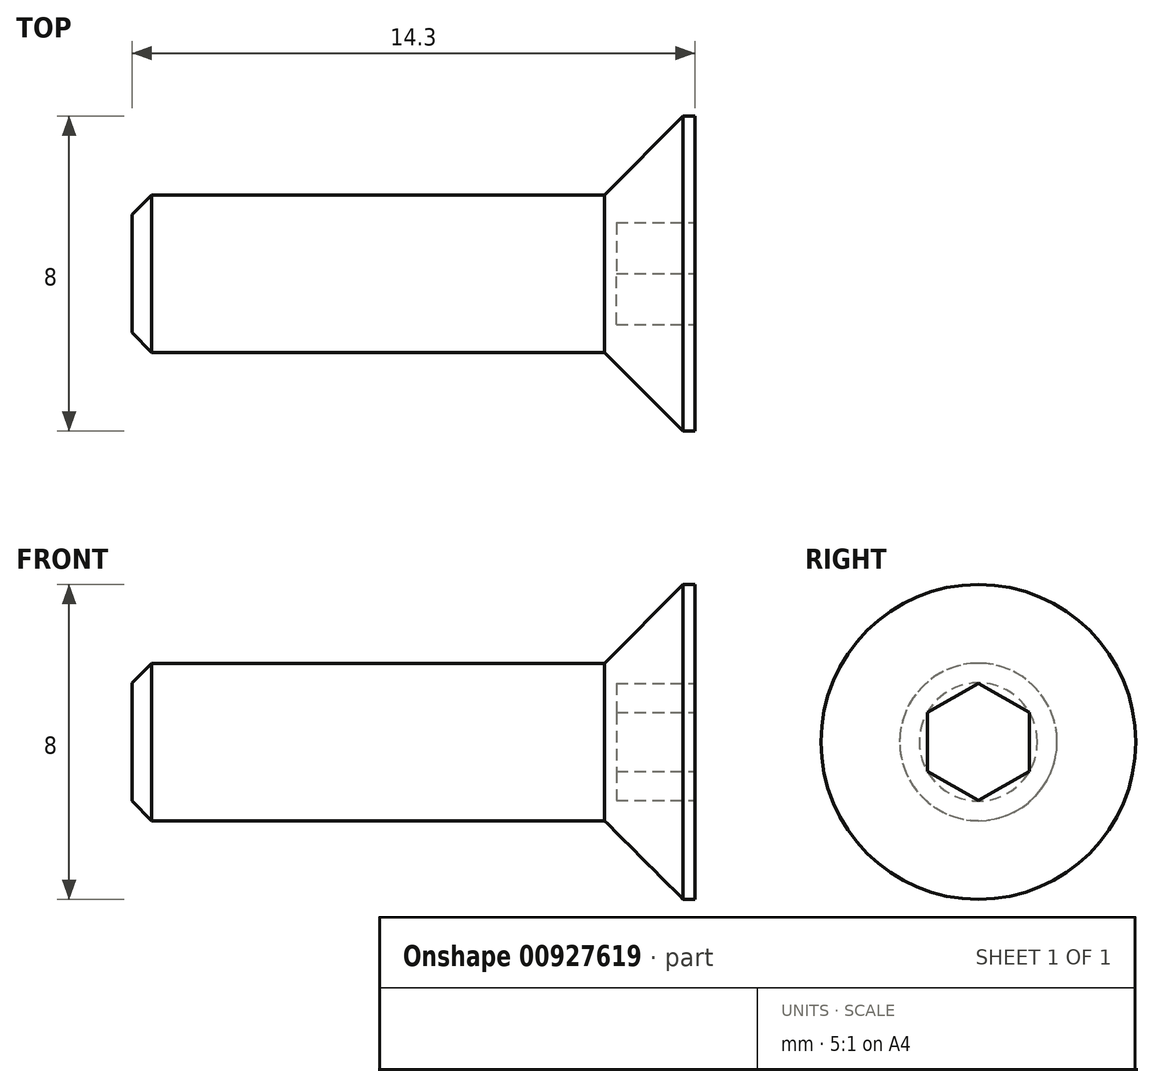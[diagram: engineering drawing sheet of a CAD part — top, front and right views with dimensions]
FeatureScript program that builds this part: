
annotation { "Feature Type Name" : "Feature", "Feature Type Description" : "" }
export const myFeature = defineFeature(function(context is Context, id is Id, definition is map)
    precondition{}
    {
        {
            var Q0;
            Q0=qCreatedBy(makeId("Right.planeOp"),FACE);
            var sketch = newSketch(context, id + "F0", { "sketchPlane" : qUnion([Q0])});
            skCircle(sketch, "E0", {"center": v(0, 0) * mm, "radius": 4 * mm});
            skSolve(sketch);
        }
        {
            var Q0;
            Q0 = qSketchRegion(id + "F0", true);
            extrude(context, id + "F1", {"entities" : qUnion([Q0]), "oppositeDirection" : true, "depth" : 2.3 * mm, "offsetDistance" : 25 * mm});
        }
        {
            var Q0;
            Q0=makeQuery(id+"F1.opExtrude","CAP_FACE",FACE,{"disambiguationData":[OSD([sQuery(id+"F0.wireOp",EDGE,"E0")])],"isStart":false});
            var sketch = newSketch(context, id + "F2", { "sketchPlane" : qUnion([Q0])});
            skCircle(sketch, "E1", {"center": v(0, 0) * mm, "radius": 2 * mm});
            skSolve(sketch);
        }
        {
            var Q0;
            Q0 = qSketchRegion(id + "F2", true);
            extrude(context, id + "F3", {"entities" : qUnion([Q0]), "operationType" : NewBodyOperationType.ADD, "depth" : 12 * mm, "offsetDistance" : 25 * mm});
        }
        {
            var Q0;
            Q0=makeQuery(id+"F3.opExtrude","CAP_EDGE",EDGE,{"disambiguationData":[OSD([sQuery(id+"F2.wireOp",EDGE,"E1")])],"isStart":false});
            chamfer(context, id + "F4", {"entities" : qUnion([Q0]), "width" : 0.5 * mm, "tangentPropagation" : true});
        }
        {
            var Q0;
            Q0=makeQuery(id+"F1.opExtrude","CAP_EDGE",EDGE,{"disambiguationData":[OSD([sQuery(id+"F0.wireOp",EDGE,"E0")])],"isStart":false});
            chamfer(context, id + "F5", {"entities" : qUnion([Q0]), "chamferType" : ChamferType.OFFSET_ANGLE, "width" : 2 * mm, "oppositeDirection" : false, "angle" : 45 * degree, "tangentPropagation" : true});
        }
        {
            var Q0;
            Q0=makeQuery(id+"F1.opExtrude","CAP_FACE",FACE,{"disambiguationData":[OSD([sQuery(id+"F0.wireOp",EDGE,"E0")])],"isStart":true});
            var sketch = newSketch(context, id + "F6", { "sketchPlane" : qUnion([Q0])});
            skLineSegment(sketch, "E2", {"start": v(0, 12.75) * mm, "end": v(0, -14.73) * mm, "construction": true});
            skLineSegment(sketch, "E3", {"start": v(-17.54, 0) * mm, "end": v(14.83, 0) * mm, "construction": true});
            skCircle(sketch, "E4.cCircle", {"center": v(0, 0) * mm, "radius": 1.29 * mm, "construction": true});
            skLineSegment(sketch, "E4.0", {"start": v(1.29, -0.74) * mm, "end": v(0, -1.49) * mm});
            skLineSegment(sketch, "E4.1", {"start": v(0, -1.49) * mm, "end": v(-1.3, -0.74) * mm});
            skLineSegment(sketch, "E4.2", {"start": v(-1.3, -0.74) * mm, "end": v(-1.29, 0.74) * mm});
            skLineSegment(sketch, "E4.3", {"start": v(-1.29, 0.74) * mm, "end": v(0, 1.49) * mm});
            skLineSegment(sketch, "E4.4", {"start": v(0, 1.49) * mm, "end": v(1.3, 0.74) * mm});
            skLineSegment(sketch, "E4.5", {"start": v(1.3, 0.74) * mm, "end": v(1.29, -0.74) * mm});
            skPoint(sketch, "E4.0.midPoint", {"position": v(0.64, -1.12) * mm});
            skSolve(sketch);
        }
        {
            var Q0;
            Q0=makeQuery(id+"F6.imprint","IMPRINT",FACE,{"disambiguationData":[TD([[makeQuery(id+"F6.imprint","IMPRINT",EDGE,{"derivedFrom":sQuery(id+"F6.wireOp",EDGE,"E4.0")}),-1.0]])]});
            extrude(context, id + "F7", {"entities" : qUnion([Q0]), "operationType" : NewBodyOperationType.REMOVE, "oppositeDirection" : true, "depth" : 2 * mm, "offsetDistance" : 25 * mm});
        }
    });
